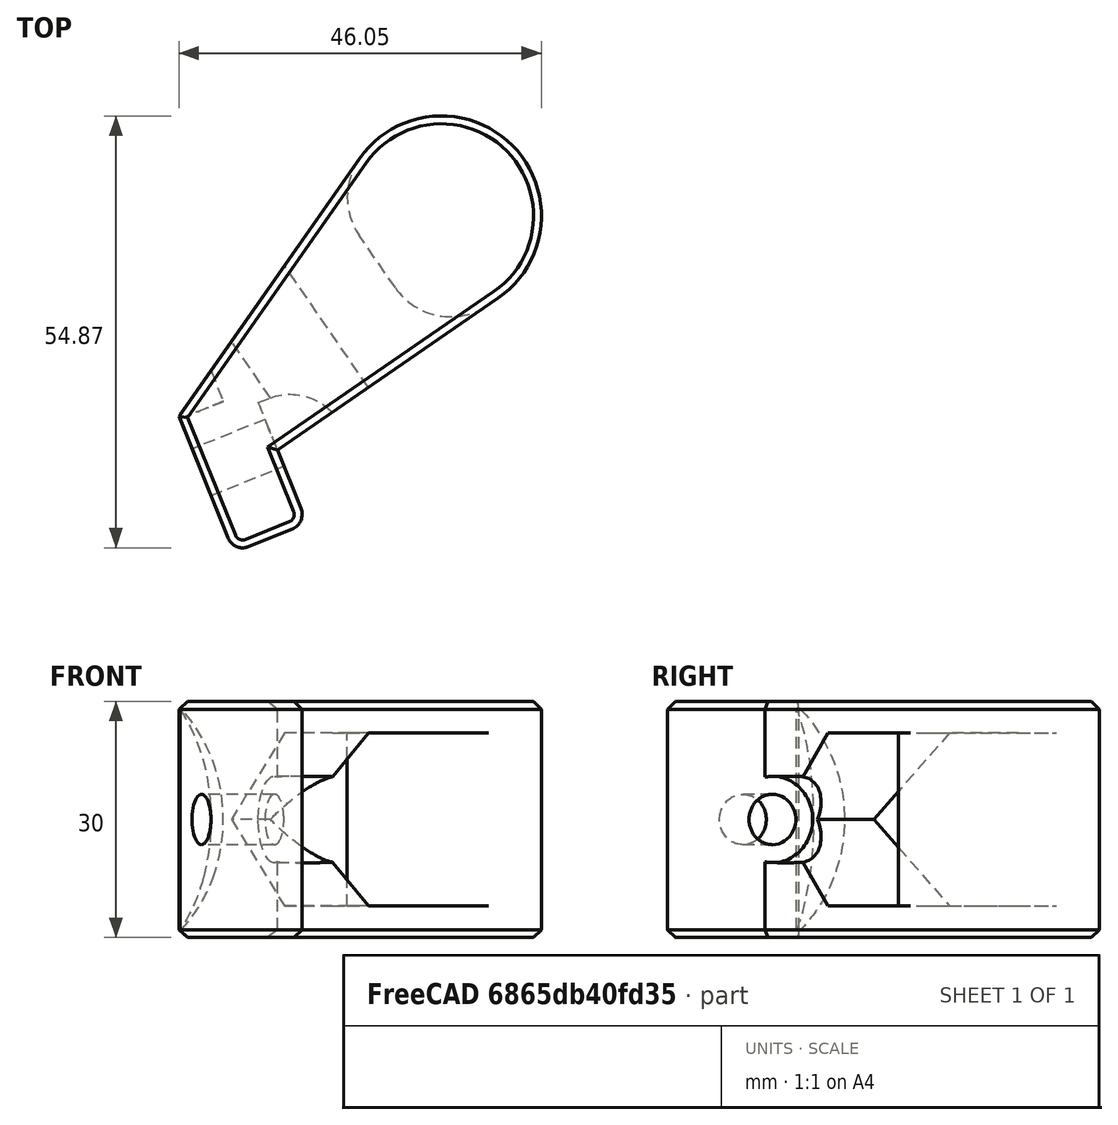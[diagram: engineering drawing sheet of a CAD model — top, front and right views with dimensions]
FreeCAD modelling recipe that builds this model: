
FCSTD DOCUMENT  (FreeCAD 0.19R)
Label: HeadLightBracket.2fcstd
License: All rights reserved
LicenseURL: http://en.wikipedia.org/wiki/All_rights_reserved
objects: Sketcher::SketchObject×4, PartDesign::Pocket×3, PartDesign::Fillet×2, PartDesign::Pad×1, Part::Cylinder×1, PartDesign::Chamfer×1, PartDesign::Body×1, Part::Cut×1, Mesh::Feature×1
note: 21 computed .brp shape members not serialized (recipe doc carries the construction recipe); baked Part::Feature solids carry a one-line shape summary decoded from their .brp

FEATURE [Sketcher::SketchObject] Sketch
  FullyConstrained = true
  MapMode = 5
  Support = -> [XY_Plane]
  sketch-geometry (6):
    g0: LineSegment StartX=33.5601 StartY=32.3107 StartZ=0 EndX=5.52577 EndY=13.0179 EndZ=0
    g1: LineSegment StartX=5.52577 StartY=13.0179 StartZ=0 EndX=9.27184 EndY=3.74607 EndZ=0
    g2: LineSegment StartX=9.27184 StartY=3.74607 StartZ=0 EndX=0 EndY=0 EndZ=0
    g3: LineSegment StartX=0 StartY=0 StartZ=0 EndX=-6.98602 EndY=17.291 EndZ=0
    g4: LineSegment StartX=-6.98602 StartY=17.291 StartZ=0 EndX=15.957 EndY=50.0571 EndZ=0
    g5: ArcOfCircle CenterX=26.3603 CenterY=42.7727 CenterZ=0 NormalX=0 NormalY=0 NormalZ=1 AngleXU=0 Radius=12.7 StartAngle=5.31514 EndAngle=8.81391
  constraints (16):
    c: Coincident(g0,g1)
    c: Coincident(g1,g2)
    c: Coincident(g2,g3)
    c: Coincident(g3,g4)
    c: Parallel(g1,g3)
    c: Angle(g1) = -1.18682
    c: Tangent(g5,g4) = 1.5708
    c: Tangent(g5,g0) = 1.5708
    c: Radius(g5) = 12.7
    c: Perpendicular(g3,g2)
    c: Distance(g2) = 10
    c: Distance(g1) = 10
    c: Coincident(g2,g-1)
    c: Distance(g0,g4) = 12.7
    c: Angle(g4) = 0.959931
    c: Distance(g4) = 40
FEATURE [PartDesign::Pad] Pad
  Direction = (1,1,1)
  Length = 30
  Length2 = 100
  Profile = -> Sketch
  Type = 0
FEATURE [Sketcher::SketchObject] Sketch001
  ExternalGeometry = -> [Pad]
  FullyConstrained = true
  MapMode = 5
  Placement = pos=(-4.30357,6.2535,0) rot=(0.91545,0.284563,0.284563;1.65902rad)
  Support = -> [Pad]
  sketch-geometry (5):
    g0: LineSegment StartX=25.9633 StartY=4 StartZ=0 EndX=14.9633 EndY=15 EndZ=0
    g1: LineSegment StartX=14.9633 StartY=15 StartZ=0 EndX=25.9633 EndY=26 EndZ=0
    g2: LineSegment StartX=25.9633 StartY=26 StartZ=0 EndX=35.9633 EndY=26 EndZ=0
    g3: LineSegment StartX=35.9633 StartY=26 StartZ=0 EndX=35.9633 EndY=4 EndZ=0
    g4: LineSegment StartX=35.9633 StartY=4 StartZ=0 EndX=25.9633 EndY=4 EndZ=0
  constraints (15):
    c: Coincident(g0,g1)
    c: DistanceY(g0) = 15
    c: Equal(g0,g1)
    c: Angle(g1) = 0.785398
    c: Coincident(g1,g2)
    c: Coincident(g2,g3)
    c: Coincident(g3,g4)
    c: Coincident(g4,g0)
    c: Vertical(g3)
    c: Horizontal(g4)
    c: Horizontal(g2)
    c: Distance(g3) = 22
    c: Distance(g3,g-3) = 10
    c: Distance(g4) = 10
    c: Distance(g2) = 10
FEATURE [Part::Cylinder] Cylinder
  Angle = 360
  AttacherType = Attacher::AttachEngine3D
  Height = 11
  Placement = pos=(-24,22,15) rot=(0.928477,0.371391,0;1.5708rad)
  Radius = 20
FEATURE [PartDesign::Pocket] Pocket
  BaseFeature = -> Pad
  Length = 5
  Length2 = 100
  Profile = -> Sketch001
  Type = 1
FEATURE [PartDesign::Fillet] Fillet
  Base = -> Pocket [Edge25,Edge6]
  BaseFeature = -> Pocket
  Radius = 8.5
  SupportTransform = false
FEATURE [Sketcher::SketchObject] Sketch002
  FullyConstrained = true
  MapMode = 5
  Placement = pos=(0,0,0) rot=(0.723589,-0.488067,-0.488067;1.88883rad)
  Support = -> [Fillet]
  sketch-geometry (1):
    g0: Circle CenterX=-11 CenterY=15 CenterZ=0 NormalX=0 NormalY=0 NormalZ=1 AngleXU=0 Radius=3.2
  constraints (3):
    c: Radius(g0) = 3.2
    c: DistanceY(g0) = 15
    c: DistanceX(g0) = -11
FEATURE [PartDesign::Pocket] Pocket001
  BaseFeature = -> Fillet
  Length = 5
  Length2 = 100
  Profile = -> Sketch002
  Type = 1
FEATURE [Sketcher::SketchObject] Sketch003
  ExternalGeometry = -> [Pocket001]
  FullyConstrained = true
  MapMode = 5
  Placement = pos=(9.27184,3.74607,0) rot=(0.430492,0.638231,0.638231;2.32857rad)
  Support = -> [Pocket001]
  sketch-geometry (1):
    g0: Circle CenterX=11 CenterY=15 CenterZ=0 NormalX=0 NormalY=0 NormalZ=1 AngleXU=0 Radius=5.5
  constraints (2):
    c: Radius(g0) = 5.5
    c: Coincident(g0,g-3)
FEATURE [PartDesign::Pocket] Pocket002
  BaseFeature = -> Pocket001
  Length = 5
  Length2 = 100
  Profile = -> Sketch003
  Reversed = true
  Type = 1
FEATURE [PartDesign::Fillet] Fillet001
  Base = -> Pocket002 [Edge22,Edge54]
  BaseFeature = -> Pocket002
  Radius = 2
  SupportTransform = false
FEATURE [PartDesign::Chamfer] Chamfer
  Angle = 45
  Base = -> Fillet001 [Face2,Face5]
  BaseFeature = -> Fillet001
  ChamferType = 0
  FlipDirection = false
  Size = 1
  Size2 = 1
  SupportTransform = false
FEATURE [PartDesign::Body] Body
  Group = -> [Sketch,Pad,Sketch001,Pocket,Fillet,Sketch002,Pocket001,Sketch003,Pocket002,Fillet001,Chamfer]
  Origin = -> Origin
  Tip = -> Chamfer
FEATURE [Part::Cut] Cut
  Base = -> Chamfer
  Tool = -> Cylinder
FEATURE [Mesh::Feature] Mesh  label="Cut (Meshed)"
